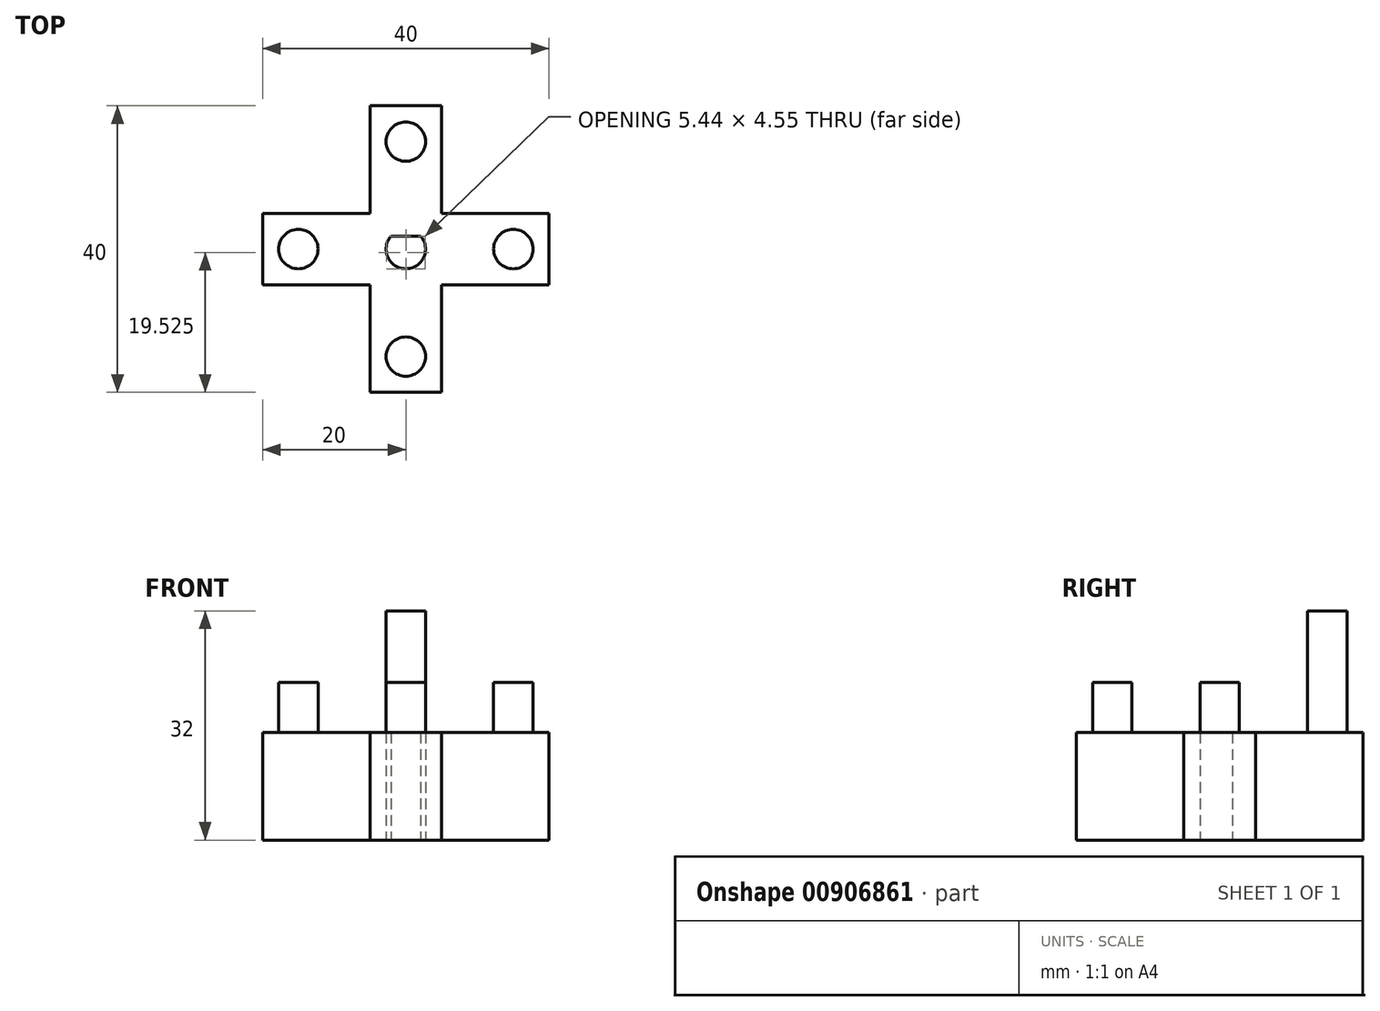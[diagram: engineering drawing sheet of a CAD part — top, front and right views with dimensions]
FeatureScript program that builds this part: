
annotation { "Feature Type Name" : "Feature", "Feature Type Description" : "" }
export const myFeature = defineFeature(function(context is Context, id is Id, definition is map)
    precondition{}
    {
        {
            var Q0;
            Q0=qCreatedBy(makeId("Top.planeOp"),FACE);
            var sketch = newSketch(context, id + "F0", { "sketchPlane" : qUnion([Q0])});
            skLineSegment(sketch, "E0.bottom", {"start": v(20, 5) * mm, "end": v(5, 5) * mm});
            skLineSegment(sketch, "E0.top", {"start": v(20, -5) * mm, "end": v(5, -5) * mm});
            skLineSegment(sketch, "E0.left", {"start": v(20, 5) * mm, "end": v(20, -5) * mm});
            skLineSegment(sketch, "E0.right", {"start": v(-20, 5) * mm, "end": v(-20, -5) * mm});
            skPoint(sketch, "E0.middle", {"position": v(0, 0) * mm});
            skLineSegment(sketch, "E1.bottom", {"start": v(5, 20) * mm, "end": v(-5, 20) * mm});
            skLineSegment(sketch, "E1.top", {"start": v(5, -20) * mm, "end": v(-5, -20) * mm});
            skLineSegment(sketch, "E1.left", {"start": v(5, 20) * mm, "end": v(5, 5) * mm});
            skLineSegment(sketch, "E1.right", {"start": v(-5, 20) * mm, "end": v(-5, 5) * mm});
            skLineSegment(sketch, "E2.trimOffspring", {"start": v(5, -5) * mm, "end": v(5, -20) * mm});
            skLineSegment(sketch, "E3.trimOffspring", {"start": v(-5, 5) * mm, "end": v(-20, 5) * mm});
            skLineSegment(sketch, "E4.trimOffspring", {"start": v(-5, -5) * mm, "end": v(-5, -20) * mm});
            skLineSegment(sketch, "E5.trimOffspring", {"start": v(-5, -5) * mm, "end": v(-20, -5) * mm});
            skCircle(sketch, "E6", {"center": v(0, 15) * mm, "radius": 2.75 * mm});
            skCircle(sketch, "E7", {"center": v(0, -15) * mm, "radius": 2.75 * mm});
            skCircle(sketch, "E8", {"center": v(-15, 0) * mm, "radius": 2.75 * mm});
            skCircle(sketch, "E9", {"center": v(15, 0) * mm, "radius": 2.75 * mm});
            skArc(sketch, "E10", {"start": v(-2.08, 1.8) * mm, "mid": v(0, -2.75) * mm, "end": v(2.08, 1.8) * mm});
            skLineSegment(sketch, "E11", {"start": v(-2.08, 1.8) * mm, "end": v(2.08, 1.8) * mm});
            skSolve(sketch);
        }
        {
            var Q0;
            Q0 = qSketchRegion(id + "F0", true);
            extrude(context, id + "F1", {"entities" : qUnion([Q0]), "depth" : 15 * mm, "offsetDistance" : 25 * mm});
        }
        {
            var Q0;
            Q0=qCreatedBy(makeId("Top.planeOp"),FACE);
            var sketch = newSketch(context, id + "F2", { "sketchPlane" : qUnion([Q0])});
            skCircle(sketch, "E12.0", {"center": v(0, 15) * mm, "radius": 2.75 * mm});
            skCircle(sketch, "E12.1", {"center": v(15, 0) * mm, "radius": 2.75 * mm});
            skCircle(sketch, "E12.2", {"center": v(0, -15) * mm, "radius": 2.75 * mm});
            skCircle(sketch, "E12.3", {"center": v(-15, 0) * mm, "radius": 2.75 * mm});
            skSolve(sketch);
        }
        {
            var Q0;
            Q0 = qSketchRegion(id + "F2", true);
            extrude(context, id + "F3", {"entities" : qUnion([Q0]), "operationType" : NewBodyOperationType.ADD, "depth" : 22 * mm, "offsetDistance" : 25 * mm});
        }
        {
            var Q0;
            Q0=makeQuery(id+"F3.opExtrude","CAP_FACE",FACE,{"disambiguationData":[OSD([sQuery(id+"F2.wireOp",EDGE,"E12.0")])],"isStart":false});
            var sketch = newSketch(context, id + "F4", { "sketchPlane" : qUnion([Q0])});
            skCircle(sketch, "E13.0", {"center": v(0, 15) * mm, "radius": 2.75 * mm});
            skSolve(sketch);
        }
        {
            var Q0;
            Q0 = qSketchRegion(id + "F4", true);
            extrude(context, id + "F5", {"entities" : qUnion([Q0]), "operationType" : NewBodyOperationType.ADD, "depth" : 10 * mm, "offsetDistance" : 25 * mm});
        }
    });
